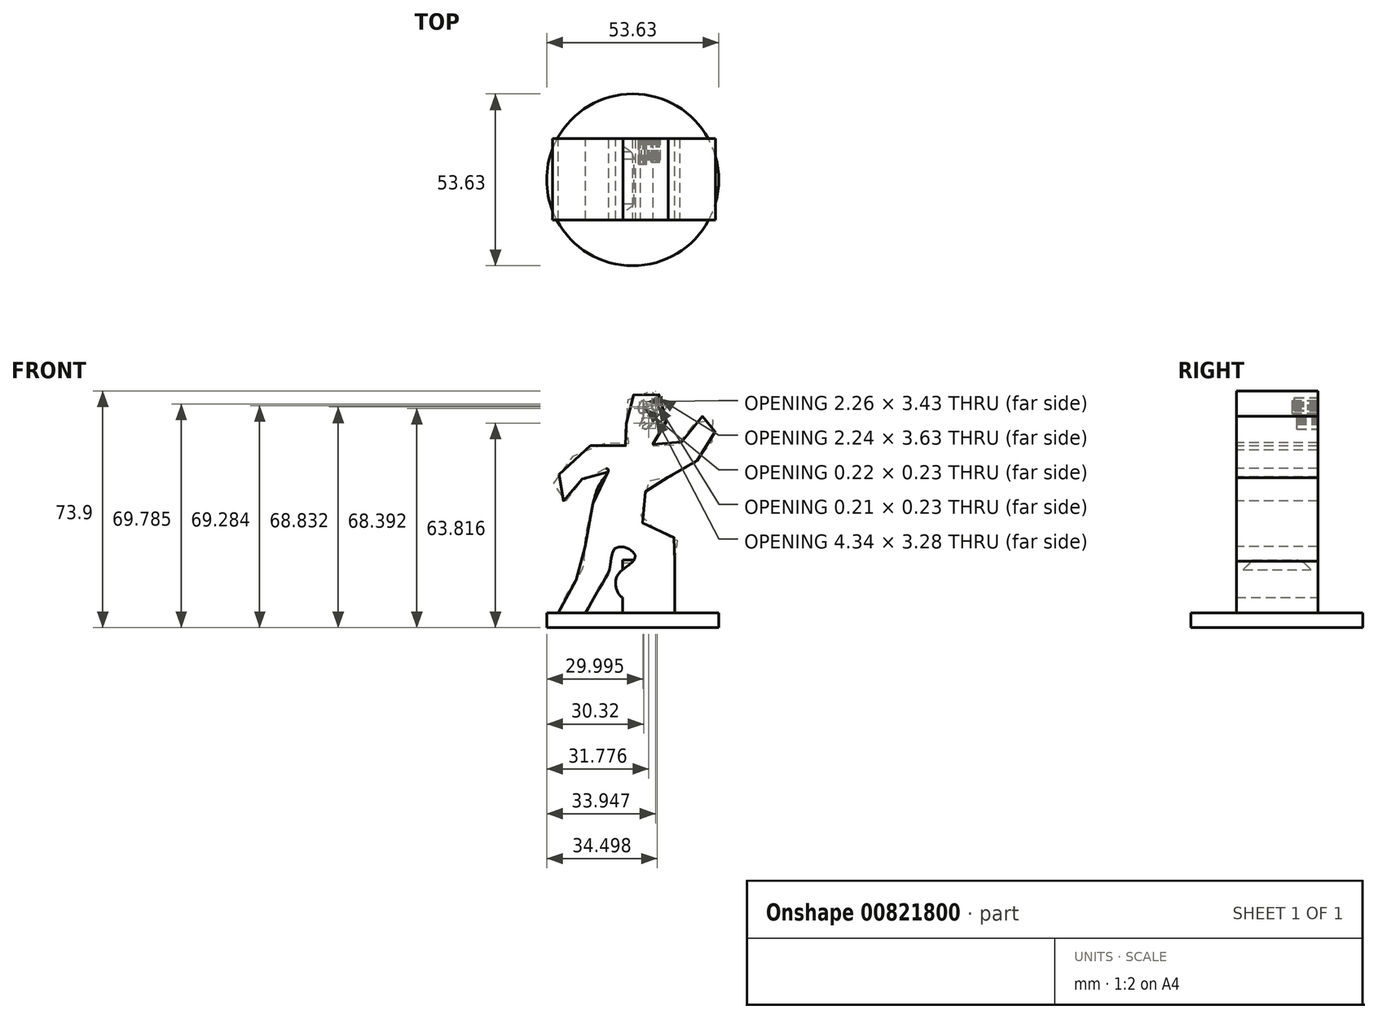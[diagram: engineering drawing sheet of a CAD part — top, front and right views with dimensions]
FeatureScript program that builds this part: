
annotation { "Feature Type Name" : "Feature", "Feature Type Description" : "" }
export const myFeature = defineFeature(function(context is Context, id is Id, definition is map)
    precondition{}
    {
        {
            var Q0;
            Q0=qCreatedBy(makeId("Front.planeOp"),FACE);
            var sketch = newSketch(context, id + "F0", { "sketchPlane" : qUnion([Q0])});
            skFitSpline(sketch, "E0", {"points": [v(-25.44, 73.74) * mm, v(-22.84, 72.35) * mm, v(-20.56, 68.34) * mm, v(-21.68, 63.1) * mm, v(-24.62, 60.46) * mm, v(-24.62, 56.02) * mm, v(-18.3, 56.56) * mm, v(-13.79, 61.04) * mm, v(-10, 65.87) * mm, v(-7.24, 65.31) * mm, v(-5.77, 63.3) * mm, v(-7.05, 57.67) * mm, v(-11.17, 52.42) * mm, v(-16.6, 48.12) * mm, v(-22.42, 46.8) * mm, v(-26.12, 46.4) * mm, v(-28.6, 36.08) * mm, v(-29.1, 33.33) * mm, v(-24.85, 31.05) * mm, v(-18.47, 28.02) * mm, v(-17.01, 25.8) * mm, v(-18.1, 21.32) * mm, v(-24.1, 15.87) * mm, v(-29.72, 11.93) * mm, v(-34.57, 9.35) * mm, v(-36.8, 14.92) * mm, v(-32.9, 19.43) * mm, v(-30.71, 22.05) * mm, v(-32.73, 24.64) * mm, v(-37.18, 24.64) * mm, v(-38.53, 19.05) * mm, v(-40.4, 14.75) * mm, v(-45.28, 6.3) * mm, v(-48.85, 2.02) * mm, v(-54.6, 1.85) * mm, v(-54.07, 6.3) * mm, v(-49.96, 13.8) * mm, v(-46.98, 19.05) * mm, v(-46.2, 27.67) * mm, v(-43.96, 38.36) * mm, v(-41.52, 45.3) * mm, v(-39.14, 49.38) * mm, v(-44.88, 48.46) * mm, v(-49.4, 42.66) * mm, v(-52.21, 39.53) * mm, v(-56.29, 42.12) * mm, v(-54.26, 48.27) * mm, v(-46.96, 55.8) * mm, v(-37.05, 57.52) * mm, v(-33.4, 56.91) * mm, v(-31.67, 60.87) * mm, v(-33.5, 63.78) * mm, v(-34.18, 69.12) * mm, v(-29.7, 73.38) * mm, v(-25.44, 73.74) * mm]});
            skSolve(sketch);
        }
        {
            var Q0;
            Q0 = qSketchRegion(id + "F0", true);
            extrude(context, id + "F1", {"entities" : qUnion([Q0]), "depth" : 25.4 * mm, "offsetDistance" : 25.4 * mm});
        }
        {
            var Q0;
            Q0=qCreatedBy(makeId("Top.planeOp"),FACE);
            var sketch = newSketch(context, id + "F2", { "sketchPlane" : qUnion([Q0])});
            skCircle(sketch, "E1", {"center": v(-31.51, -12.8) * mm, "radius": 26.82 * mm});
            skSolve(sketch);
        }
        {
            var Q0;
            Q0 = qSketchRegion(id + "F2", true);
            extrude(context, id + "F3", {"entities" : qUnion([Q0]), "operationType" : NewBodyOperationType.ADD, "depth" : 4.57 * mm, "offsetDistance" : 25.4 * mm});
        }
        {
            var Q0;
            Q0=qCreatedBy(makeId("Front.planeOp"),FACE);
            var sketch = newSketch(context, id + "F4", { "sketchPlane" : qUnion([Q0])});
            skLineSegment(sketch, "E2.bottom", {"start": v(-18.47, 21.08) * mm, "end": v(-34.7, 21.08) * mm});
            skLineSegment(sketch, "E2.top", {"start": v(-18.47, 4.64) * mm, "end": v(-34.7, 4.64) * mm});
            skLineSegment(sketch, "E2.left", {"start": v(-18.47, 21.08) * mm, "end": v(-18.47, 4.64) * mm});
            skLineSegment(sketch, "E2.right", {"start": v(-34.7, 21.08) * mm, "end": v(-34.7, 4.64) * mm});
            skSolve(sketch);
        }
        {
            var Q0;
            Q0 = qSketchRegion(id + "F4", true);
            extrude(context, id + "F5", {"entities" : qUnion([Q0]), "operationType" : NewBodyOperationType.ADD, "depth" : 25.4 * mm, "offsetDistance" : 25.4 * mm});
        }
        {
            var Q0;
            Q0=makeQuery(id+"F5.opExtrude","CAP_EDGE",EDGE,{"disambiguationData":[OSD([sQuery(id+"F4.wireOp",EDGE,"E2.bottom")])],"isStart":true});
            chamfer(context, id + "F6", {"entities" : qUnion([Q0]), "width" : 5.08 * mm, "tangentPropagation" : true});
        }
        {
            var Q0;
            Q0=makeQuery(id+"F5.opExtrude","CAP_EDGE",EDGE,{"disambiguationData":[OSD([sQuery(id+"F4.wireOp",EDGE,"E2.bottom")])],"isStart":false});
            chamfer(context, id + "F7", {"entities" : qUnion([Q0]), "width" : 5.08 * mm, "tangentPropagation" : true});
        }
        {
            var Q0;
            {var subQ0=sQuery(id+"F4.wireOp",EDGE,"E2.bottom");Q0=makeQuery(id+"F6.opChamfer","BLEND_EDGE",EDGE,{"blendedFrom":[makeQuery(id+"F5.opExtrude","CAP_EDGE",EDGE,{"disambiguationData":[OSD([subQ0])],"isStart":true}),makeQuery(id+"F5.opExtrude","SWEPT_FACE",FACE,{"disambiguationData":[OSD([subQ0])]})],"blendedInto":[makeQuery(id+"F5.opExtrude","SWEPT_FACE",FACE,{"disambiguationData":[OSD([subQ0])]})]});}
            chamfer(context, id + "F8", {"entities" : qUnion([Q0]), "width" : 3.14 * mm, "tangentPropagation" : true});
        }
        {
            var Q0;
            Q0=makeQuery(id+"F5.boolean.opBoolean","MERGE",FACE,{"derivedFrom":[makeQuery(id+"F1.opExtrude","CAP_FACE",FACE,{"disambiguationData":[OSD([sQuery(id+"F0.wireOp",EDGE,"E0")])],"isStart":true}),makeQuery(id+"F5.opExtrude","CAP_FACE",FACE,{"disambiguationData":[OSD([sQuery(id+"F4.wireOp",EDGE,"E2.bottom"),sQuery(id+"F4.wireOp",EDGE,"E2.top"),sQuery(id+"F4.wireOp",EDGE,"E2.left"),sQuery(id+"F4.wireOp",EDGE,"E2.right")])],"isStart":true})]});
            var sketch = newSketch(context, id + "F9", { "sketchPlane" : qUnion([Q0])});
            skFitSpline(sketch, "E3", {"points": [v(23.26, 70.5) * mm, v(23.34, 70.8) * mm, v(23.48, 71.12) * mm, v(23.72, 71.45) * mm, v(23.9, 71.58) * mm, v(24.05, 71.63) * mm, v(24.47, 71.6) * mm, v(24.87, 71.3) * mm, v(25.15, 70.94) * mm, v(25.32, 70.54) * mm, v(25.47, 69.84) * mm, v(25.5, 69.3) * mm, v(25.37, 68.64) * mm, v(25.01, 68.07) * mm, v(24.68, 67.9) * mm, v(24.21, 67.95) * mm, v(23.77, 68.31) * mm, v(23.44, 68.83) * mm, v(23.21, 69.88) * mm, v(23.26, 70.5) * mm]});
            skFitSpline(sketch, "E4", {"points": [v(23.26, 70.7) * mm, v(23.28, 70.84) * mm, v(23.37, 71.08) * mm, v(23.45, 71.24) * mm, v(23.57, 71.45) * mm, v(23.75, 71.67) * mm, v(24, 71.8) * mm, v(24.23, 71.86) * mm, v(24.59, 71.82) * mm, v(25, 71.54) * mm, v(25.32, 71.12) * mm, v(25.73, 70.2) * mm, v(25.78, 69.16) * mm, v(25.7, 68.76) * mm, v(25.5, 68.25) * mm, v(25.2, 67.83) * mm, v(24.87, 67.65) * mm, v(24.47, 67.65) * mm, v(23.87, 67.99) * mm, v(23.48, 68.57) * mm, v(23.26, 69.19) * mm, v(23.24, 69.28) * mm, v(23.18, 69.75) * mm, v(23.17, 70) * mm, v(23.18, 70.12) * mm, v(23.19, 70.27) * mm, v(23.21, 70.59) * mm, v(23.26, 70.7) * mm]});
            skFitSpline(sketch, "E5", {"points": [v(23.9, 70) * mm, v(23.9, 69.95) * mm, v(24.05, 69.88) * mm, v(24.13, 69.88) * mm, v(24.15, 69.76) * mm, v(24.15, 69.38) * mm, v(24.05, 69.16) * mm, v(23.96, 69.05) * mm, v(23.77, 68.99) * mm, v(23.58, 69.09) * mm, v(23.39, 69.38) * mm, v(23.34, 69.74) * mm, v(23.37, 70.06) * mm, v(23.48, 70.29) * mm, v(23.63, 70.38) * mm, v(23.84, 70.37) * mm, v(23.81, 70.33) * mm, v(23.8, 70.17) * mm, v(23.9, 70) * mm]});
            skFitSpline(sketch, "E6", {"points": [v(23.73, 69.32) * mm, v(23.74, 69.35) * mm, v(23.76, 69.4) * mm, v(23.85, 69.4) * mm, v(23.92, 69.35) * mm, v(23.94, 69.26) * mm, v(23.92, 69.17) * mm, v(23.84, 69.17) * mm, v(23.73, 69.25) * mm, v(23.73, 69.32) * mm]});
            skSolve(sketch);
        }
        {
            var Q0;
            Q0=makeQuery(id+"F9.imprint","IMPRINT",FACE,{"disambiguationData":[TD([[makeQuery(id+"F9.imprint","IMPRINT",EDGE,{"derivedFrom":sQuery(id+"F9.wireOp",EDGE,"E3")}),1.0]])]});
            var Q1;
            Q1=makeQuery(id+"F9.imprint","IMPRINT",FACE,{"disambiguationData":[TD([[makeQuery(id+"F9.imprint","IMPRINT",EDGE,{"derivedFrom":sQuery(id+"F9.wireOp",EDGE,"E5")}),-1.0]])]});
            extrude(context, id + "F10", {"entities" : qUnion([Q0, Q1]), "oppositeDirection" : true, "depth" : 7.3 * mm, "offsetDistance" : 25.4 * mm});
        }
        {
            var Q0;
            Q0=makeQuery(id+"F5.boolean.opBoolean","MERGE",FACE,{"derivedFrom":[makeQuery(id+"F1.opExtrude","CAP_FACE",FACE,{"disambiguationData":[OSD([sQuery(id+"F0.wireOp",EDGE,"E0")])],"isStart":true}),makeQuery(id+"F5.opExtrude","CAP_FACE",FACE,{"disambiguationData":[OSD([sQuery(id+"F4.wireOp",EDGE,"E2.bottom"),sQuery(id+"F4.wireOp",EDGE,"E2.top"),sQuery(id+"F4.wireOp",EDGE,"E2.left"),sQuery(id+"F4.wireOp",EDGE,"E2.right")])],"isStart":true})]});
            var sketch = newSketch(context, id + "F11", { "sketchPlane" : qUnion([Q0])});
            skFitSpline(sketch, "E7", {"points": [v(28, 69.45) * mm, v(27.97, 69.43) * mm, v(27.96, 69.38) * mm, v(27.95, 69.3) * mm, v(27.98, 69.18) * mm, v(28.1, 69.04) * mm, v(28.2, 68.99) * mm, v(28.3, 69) * mm, v(28.34, 68.73) * mm, v(28.3, 68.45) * mm, v(28.24, 68.26) * mm, v(28.03, 68.1) * mm, v(27.83, 68.1) * mm, v(27.6, 68.4) * mm, v(27.49, 68.7) * mm, v(27.5, 69.09) * mm, v(27.6, 69.35) * mm, v(27.73, 69.49) * mm, v(28, 69.45) * mm]});
            skFitSpline(sketch, "E8", {"points": [v(27.95, 68.5) * mm, v(27.91, 68.49) * mm, v(27.9, 68.42) * mm, v(27.9, 68.37) * mm, v(27.94, 68.32) * mm, v(27.98, 68.29) * mm, v(28.08, 68.28) * mm, v(28.12, 68.32) * mm, v(28.12, 68.41) * mm, v(28.06, 68.5) * mm, v(27.95, 68.5) * mm]});
            skFitSpline(sketch, "E9", {"points": [v(29.47, 68.44) * mm, v(29.47, 68.7) * mm, v(29.44, 69.08) * mm, v(29.3, 69.6) * mm, v(29.07, 70.08) * mm, v(28.92, 70.37) * mm, v(28.44, 70.72) * mm, v(27.81, 70.65) * mm, v(27.41, 70.15) * mm, v(27.32, 69.9) * mm, v(27.24, 69.6) * mm, v(27.2, 69.2) * mm, v(27.23, 68.66) * mm, v(27.3, 68.37) * mm, v(27.42, 67.96) * mm, v(27.66, 67.51) * mm, v(27.93, 67.21) * mm, v(28.25, 67.04) * mm, v(28.53, 66.99) * mm, v(28.91, 67.14) * mm, v(29.34, 67.77) * mm, v(29.47, 68.44) * mm]});
            skFitSpline(sketch, "E10", {"points": [v(28.76, 66.74) * mm, v(29.07, 66.84) * mm, v(29.3, 67.12) * mm, v(29.47, 67.3) * mm, v(29.69, 68.05) * mm, v(29.72, 68.73) * mm, v(29.63, 69.49) * mm, v(29.47, 69.96) * mm, v(29.24, 70.34) * mm, v(28.92, 70.72) * mm, v(28.62, 70.9) * mm, v(28.2, 70.97) * mm, v(27.81, 70.84) * mm, v(27.38, 70.3) * mm, v(27.24, 69.95) * mm, v(27.17, 69.49) * mm, v(27.14, 69.08) * mm, v(27.16, 68.82) * mm, v(27.24, 68.26) * mm, v(27.37, 67.87) * mm, v(27.56, 67.5) * mm, v(27.7, 67.3) * mm, v(27.93, 66.99) * mm, v(28.44, 66.72) * mm, v(28.76, 66.74) * mm]});
            skSolve(sketch);
        }
        {
            var Q0;
            Q0=makeQuery(id+"F11.imprint","IMPRINT",FACE,{"disambiguationData":[TD([[makeQuery(id+"F11.imprint","IMPRINT",EDGE,{"derivedFrom":sQuery(id+"F11.wireOp",EDGE,"E9")}),-1.0]])]});
            var Q1;
            Q1=makeQuery(id+"F11.imprint","IMPRINT",FACE,{"disambiguationData":[TD([[makeQuery(id+"F11.imprint","IMPRINT",EDGE,{"derivedFrom":sQuery(id+"F11.wireOp",EDGE,"E7")}),-1.0]])]});
            extrude(context, id + "F12", {"entities" : qUnion([Q0, Q1]), "oppositeDirection" : true, "depth" : 8 * mm, "offsetDistance" : 25.4 * mm});
        }
        {
            var Q0;
            Q0=makeQuery(id+"F5.boolean.opBoolean","MERGE",FACE,{"derivedFrom":[makeQuery(id+"F1.opExtrude","CAP_FACE",FACE,{"disambiguationData":[OSD([sQuery(id+"F0.wireOp",EDGE,"E0")])],"isStart":true}),makeQuery(id+"F5.opExtrude","CAP_FACE",FACE,{"disambiguationData":[OSD([sQuery(id+"F4.wireOp",EDGE,"E2.bottom"),sQuery(id+"F4.wireOp",EDGE,"E2.top"),sQuery(id+"F4.wireOp",EDGE,"E2.left"),sQuery(id+"F4.wireOp",EDGE,"E2.right")])],"isStart":true})]});
            var sketch = newSketch(context, id + "F13", { "sketchPlane" : qUnion([Q0])});
            skFitSpline(sketch, "E11", {"points": [v(24.27, 66.33) * mm, v(24.28, 66.27) * mm, v(24.3, 66.15) * mm, v(24.41, 65.96) * mm, v(24.59, 65.8) * mm, v(24.7, 65.72) * mm, v(24.88, 65.65) * mm, v(25.18, 65.6) * mm, v(25.44, 65.62) * mm, v(25.96, 65.73) * mm, v(26.48, 65.91) * mm, v(26.75, 66.02) * mm, v(27.1, 66.1) * mm, v(27.4, 66.14) * mm, v(27.72, 66.06) * mm, v(27.98, 65.74) * mm, v(28.45, 65.07) * mm, v(29.06, 64.04) * mm, v(29.47, 63.16) * mm, v(29.52, 63) * mm, v(29.47, 62.8) * mm, v(29.06, 62.5) * mm, v(28.12, 62.02) * mm, v(27.64, 61.85) * mm, v(27.52, 61.85) * mm, v(27.24, 62.06) * mm, v(26.45, 62.66) * mm, v(25.73, 63.1) * mm, v(25.32, 63.31) * mm, v(24.8, 63.51) * mm, v(24.36, 63.64) * mm, v(23.8, 63.7) * mm, v(23.35, 63.63) * mm, v(23.06, 63.49) * mm, v(22.96, 63.49) * mm, v(22.9, 63.57) * mm, v(22.9, 63.66) * mm, v(23.3, 63.84) * mm, v(23.47, 63.85) * mm, v(23.45, 63.97) * mm, v(23.57, 64.4) * mm, v(23.77, 64.73) * mm, v(23.97, 64.97) * mm, v(24.25, 65.25) * mm, v(24.33, 65.3) * mm, v(24.52, 65.2) * mm, v(24.89, 64.96) * mm, v(25.2, 64.75) * mm, v(25.25, 64.75) * mm, v(25.23, 64.79) * mm, v(25.07, 65) * mm, v(24.88, 65.3) * mm, v(24.81, 65.43) * mm, v(24.76, 65.5) * mm, v(24.61, 65.57) * mm, v(24.32, 65.79) * mm, v(24.17, 66.04) * mm, v(24.07, 66.28) * mm, v(24.11, 66.4) * mm, v(24.22, 66.41) * mm, v(24.27, 66.33) * mm]});
            skFitSpline(sketch, "E12", {"points": [v(25.03, 65.44) * mm, v(25.45, 64.74) * mm, v(25.61, 64.45) * mm, v(25.6, 64.36) * mm, v(25.5, 64.33) * mm, v(24.96, 64.7) * mm, v(24.88, 64.74) * mm, v(24.78, 64.54) * mm, v(24.78, 64.34) * mm, v(24.68, 64.3) * mm, v(24.58, 64.37) * mm, v(24.58, 64.65) * mm, v(24.7, 64.86) * mm, v(24.67, 64.9) * mm, v(24.47, 65.02) * mm, v(24.4, 65.07) * mm, v(24.28, 64.97) * mm, v(23.9, 64.54) * mm, v(23.7, 64.09) * mm, v(23.67, 63.9) * mm, v(23.78, 63.9) * mm, v(24.25, 63.86) * mm, v(24.62, 63.78) * mm, v(25.16, 63.58) * mm, v(25.77, 63.28) * mm, v(26.64, 62.72) * mm, v(27.34, 62.23) * mm, v(27.53, 62.06) * mm, v(27.6, 62.05) * mm, v(28.13, 62.26) * mm, v(28.42, 62.38) * mm, v(28.68, 62.5) * mm, v(28.69, 62.76) * mm, v(28.17, 63.2) * mm, v(27.48, 63.58) * mm, v(27.26, 63.76) * mm, v(27.08, 63.76) * mm, v(26.8, 63.6) * mm, v(26.68, 63.57) * mm, v(26.58, 63.69) * mm, v(26.77, 63.87) * mm, v(26.57, 63.92) * mm, v(26.36, 63.95) * mm, v(26.36, 64.13) * mm, v(26.7, 64.04) * mm, v(26.74, 64.19) * mm, v(26.75, 64.39) * mm, v(26.77, 64.47) * mm, v(26.92, 64.47) * mm, v(26.95, 64.04) * mm, v(27.06, 64.04) * mm, v(27.24, 63.95) * mm, v(27.56, 63.9) * mm, v(27.55, 64.04) * mm, v(27.56, 64.27) * mm, v(27.72, 64.3) * mm, v(27.76, 64.04) * mm, v(27.76, 63.85) * mm, v(28.15, 63.77) * mm, v(28.63, 63.65) * mm, v(28.78, 63.62) * mm, v(28.8, 63.66) * mm, v(28.8, 63.93) * mm, v(28.79, 64.1) * mm, v(28.77, 64.14) * mm, v(28.66, 64.32) * mm, v(28.28, 64.96) * mm, v(28, 65.38) * mm, v(27.87, 65.56) * mm, v(27.82, 65.58) * mm, v(27.66, 65.56) * mm, v(27.55, 65.5) * mm, v(27.52, 65.4) * mm, v(27.42, 65.34) * mm, v(27.2, 65.39) * mm, v(26.9, 65.52) * mm, v(26.55, 65.58) * mm, v(26.3, 65.57) * mm, v(26.02, 65.54) * mm, v(25.88, 65.48) * mm, v(25.58, 65.43) * mm, v(25.2, 65.41) * mm, v(25.03, 65.44) * mm]});
            skSolve(sketch);
        }
        {
            var Q0;
            Q0=makeQuery(id+"F13.imprint","IMPRINT",FACE,{"disambiguationData":[TD([[makeQuery(id+"F13.imprint","IMPRINT",EDGE,{"derivedFrom":sQuery(id+"F13.wireOp",EDGE,"E11")}),-1.0]])]});
            extrude(context, id + "F14", {"entities" : qUnion([Q0]), "oppositeDirection" : true, "depth" : 6.55 * mm, "offsetDistance" : 25.4 * mm});
        }
    });
